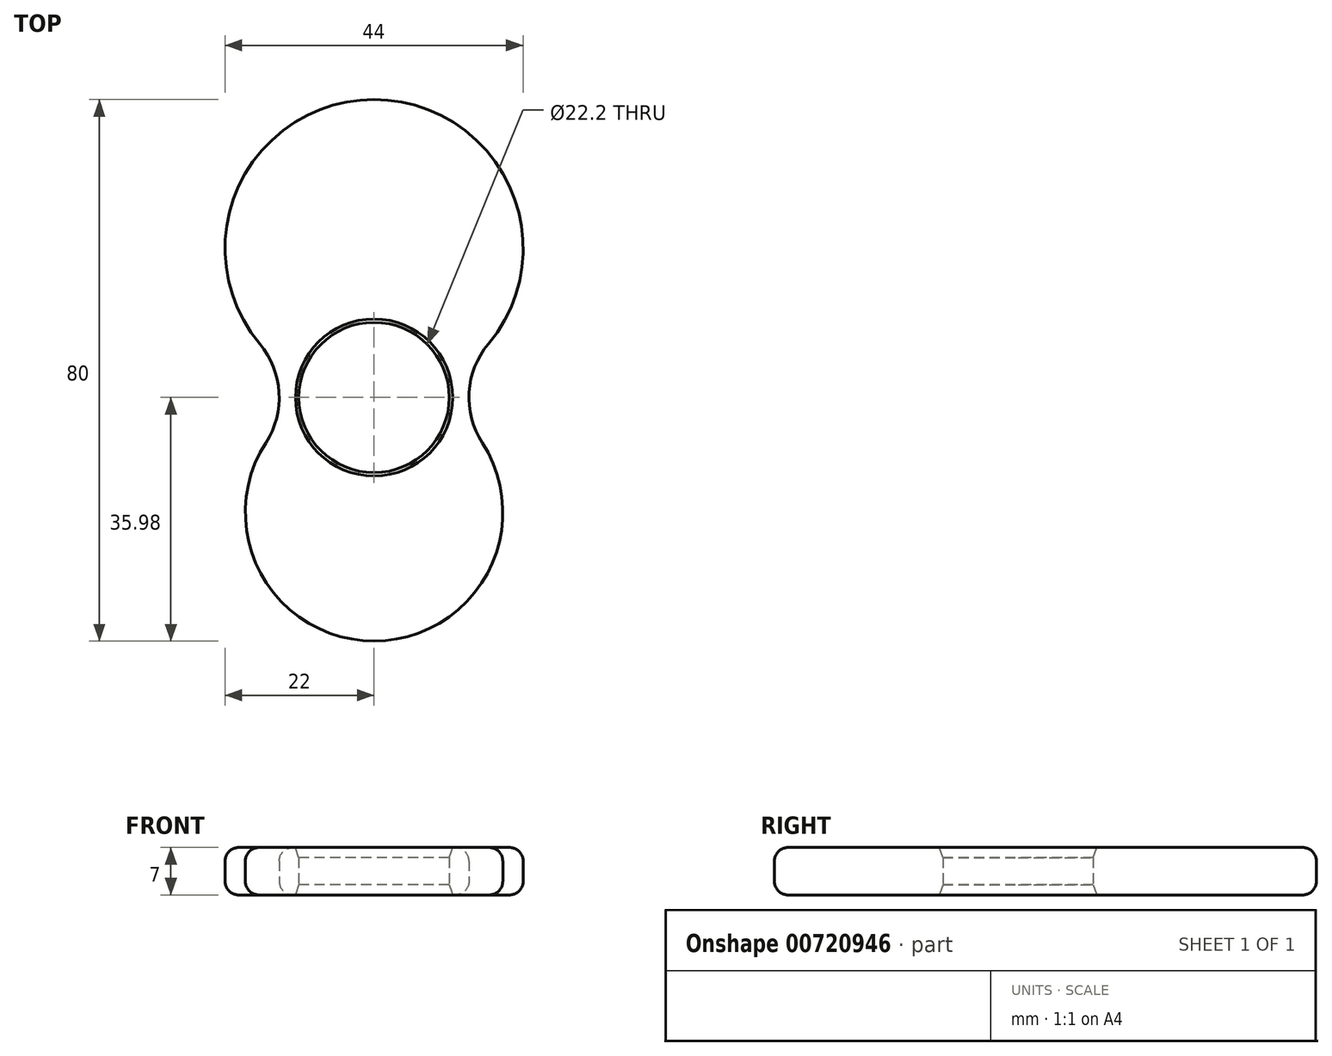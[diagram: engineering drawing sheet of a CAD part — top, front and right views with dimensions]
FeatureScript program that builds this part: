
annotation { "Feature Type Name" : "Feature", "Feature Type Description" : "" }
export const myFeature = defineFeature(function(context is Context, id is Id, definition is map)
    precondition{}
    {
        {
            var Q0;
            Q0=qCreatedBy(makeId("Top.planeOp"),FACE);
            var sketch = newSketch(context, id + "F0", { "sketchPlane" : qUnion([Q0])});
            skLineSegment(sketch, "E0", {"start": v(0, 0) * mm, "end": v(-28, 0) * mm, "construction": true});
            skArc(sketch, "E1", {"start": v(-29.97, -6.68) * mm, "mid": v(-28.02, 0.76) * mm, "end": v(-30.87, 7.9) * mm});
            skArc(sketch, "E2", {"start": v(2.87, 7.9) * mm, "mid": v(0.02, 0.76) * mm, "end": v(1.97, -6.68) * mm});
            skArc(sketch, "E3", {"start": v(2.87, 7.9) * mm, "mid": v(-14, 44.02) * mm, "end": v(-30.87, 7.9) * mm});
            skArc(sketch, "E4", {"start": v(-29.97, -6.68) * mm, "mid": v(-14, -35.98) * mm, "end": v(1.97, -6.68) * mm});
            skLineSegment(sketch, "E5", {"start": v(-36, 22.02) * mm, "end": v(8, 22.02) * mm, "construction": true});
            skLineSegment(sketch, "E6", {"start": v(-14, 44.02) * mm, "end": v(-14, -35.98) * mm, "construction": true});
            skCircle(sketch, "E7", {"center": v(-14, 0) * mm, "radius": 11.1 * mm});
            skLineSegment(sketch, "E8", {"start": v(-33, -16.98) * mm, "end": v(5, -16.98) * mm});
            skSolve(sketch);
        }
        {
            var Q0;
            Q0=makeQuery(id+"F0.imprint","IMPRINT",FACE,{"disambiguationData":[TD([[makeQuery(id+"F0.imprint","IMPRINT",EDGE,{"derivedFrom":sQuery(id+"F0.wireOp",EDGE,"E1")}),-1.0]])]});
            var Q1;
            {var subQ0=sQuery(id+"F0.wireOp",EDGE,"E8");Q1=makeQuery(id+"F0.imprint","IMPRINT",FACE,{"disambiguationData":[TD([[makeQuery(id+"F0.imprint","IMPRINT",EDGE,{"derivedFrom":subQ0}),-1.0]])]});}
            extrude(context, id + "F1", {"entities" : qUnion([Q0, Q1]), "depth" : 7 * mm});
        }
        {
            var Q0;
            Q0=makeQuery(id+"F1.opExtrude","CAP_EDGE",EDGE,{"disambiguationData":[OSD([sQuery(id+"F0.wireOp",EDGE,"E7")])],"isStart":false});
            var Q1;
            Q1=makeQuery(id+"F1.opExtrude","CAP_EDGE",EDGE,{"disambiguationData":[OSD([sQuery(id+"F0.wireOp",EDGE,"E7")])],"isStart":true});
            chamfer(context, id + "F2", {"entities" : qUnion([Q0, Q1]), "chamferType" : ChamferType.TWO_OFFSETS, "width1" : 1.5 * mm, "oppositeDirection" : false, "width2" : .5 * mm, "tangentPropagation" : true});
        }
        {
            var Q0;
            Q0=makeQuery(id+"F1.opExtrude","CAP_EDGE",EDGE,{"disambiguationData":[OSD([sQuery(id+"F0.wireOp",EDGE,"E4")])],"isStart":false});
            var Q1;
            Q1=makeQuery(id+"F1.opExtrude","CAP_EDGE",EDGE,{"disambiguationData":[OSD([sQuery(id+"F0.wireOp",EDGE,"E4")])],"isStart":true});
            fillet(context, id + "F3", {"entities" : qUnion([Q0, Q1]), "radius" : 2 * mm, "tangentPropagation" : true, "allowEdgeOverflow" : false});
        }
    });
